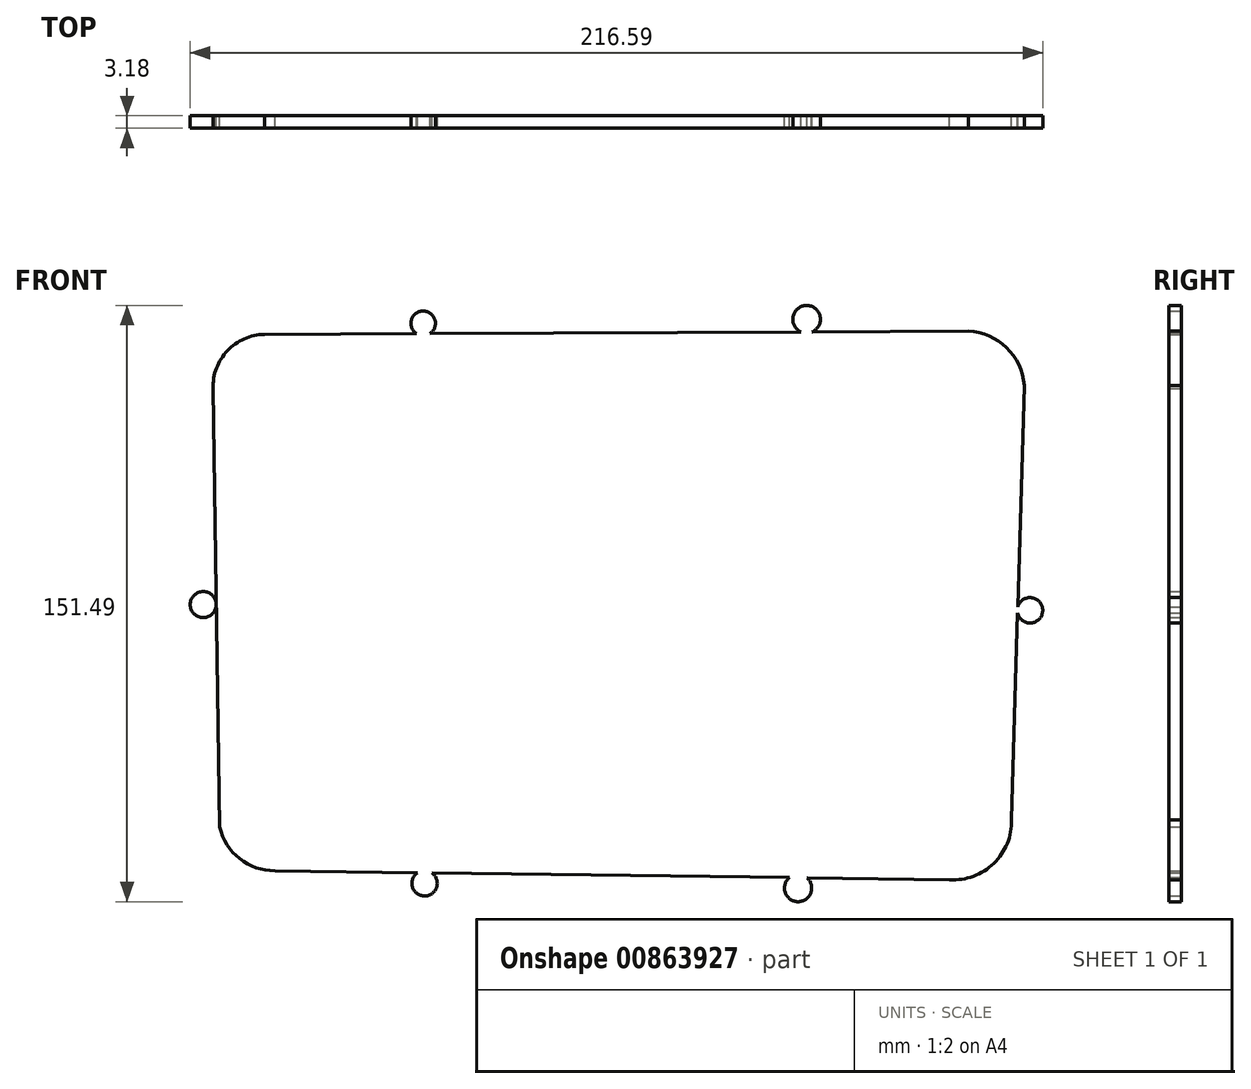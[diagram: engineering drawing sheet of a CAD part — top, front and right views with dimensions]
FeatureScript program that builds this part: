
annotation { "Feature Type Name" : "Feature", "Feature Type Description" : "" }
export const myFeature = defineFeature(function(context is Context, id is Id, definition is map)
    precondition{}
    {
        {
            var Q0;
            Q0=qCreatedBy(makeId("Front.planeOp"),FACE);
            var sketch = newSketch(context, id + "F0", { "sketchPlane" : qUnion([Q0])});
            skLineSegment(sketch, "E0", {"start": v(124.3, 5.43) * mm, "end": v(-78.9, 5.7) * mm});
            skCircle(sketch, "E1", {"center": v(-75.4, -27.49) * mm, "radius": 3.31 * mm});
            skCircle(sketch, "E2", {"center": v(-19.52, 43.96) * mm, "radius": 3.13 * mm});
            skCircle(sketch, "E3", {"center": v(77.89, 45) * mm, "radius": 3.51 * mm});
            skCircle(sketch, "E4", {"center": v(134.65, -28.95) * mm, "radius": 3.23 * mm});
            skCircle(sketch, "E5", {"center": v(-19.17, -98.3) * mm, "radius": 3.23 * mm});
            skCircle(sketch, "E6", {"center": v(75.72, -99.53) * mm, "radius": 3.46 * mm});
            skArc(sketch, "E7", {"start": v(-71.23, -83.96) * mm, "mid": v(-66.17, -92.03) * mm, "end": v(-57.17, -95.12) * mm});
            skArc(sketch, "E8", {"start": v(-59.87, 41.16) * mm, "mid": v(-69.27, 37) * mm, "end": v(-72.9, 27.37) * mm});
            skArc(sketch, "E9", {"start": v(133.18, 28.22) * mm, "mid": v(128.68, 37.78) * mm, "end": v(118.98, 41.96) * mm});
            skArc(sketch, "E10", {"start": v(114.22, -97.4) * mm, "mid": v(125.43, -93.25) * mm, "end": v(129.94, -82.18) * mm});
            skLineSegment(sketch, "E11", {"start": v(-57.17, -95.12) * mm, "end": v(114.22, -97.4) * mm});
            skLineSegment(sketch, "E12", {"start": v(-71.23, -83.96) * mm, "end": v(-72.9, 27.37) * mm});
            skLineSegment(sketch, "E13", {"start": v(-59.87, 41.16) * mm, "end": v(118.98, 41.96) * mm});
            skLineSegment(sketch, "E14", {"start": v(133.18, 28.22) * mm, "end": v(129.94, -82.18) * mm});
            skSolve(sketch);
        }
        {
            var Q0;
            Q0 = qSketchRegion(id + "F0", true);
            extrude(context, id + "F1", {"entities" : qUnion([Q0]), "depth" : 3.17 * mm, "offsetDistance" : 25.4 * mm});
        }
    });
